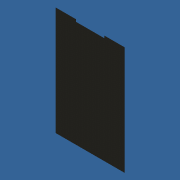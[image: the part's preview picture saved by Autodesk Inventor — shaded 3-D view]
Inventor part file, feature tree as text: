
AUTODESK INVENTOR PART (.ipt)
format: ipt  version: unknown  size: 165,888 bytes
history: native  units: in
note: dims shown in document units (in); Inventor stores cm internally (conversion verified against a paired STEP export)
features: extrude x1, sketch x1
ambient origin geometry x8: Origin, YZ Plane, XZ Plane, XY Plane, X Axis, Y Axis, Z Axis, Center Point
bodies: Solid1 (feature_tree)
feature tree (2):
  extrude  "Extrusion1"  Depth=38.0in
  sketch  "Sketch1"  dims[d0=91.0in d1=38.0in d2=144.0in d3=3.0in d4=0.125in d5=0.0in]
